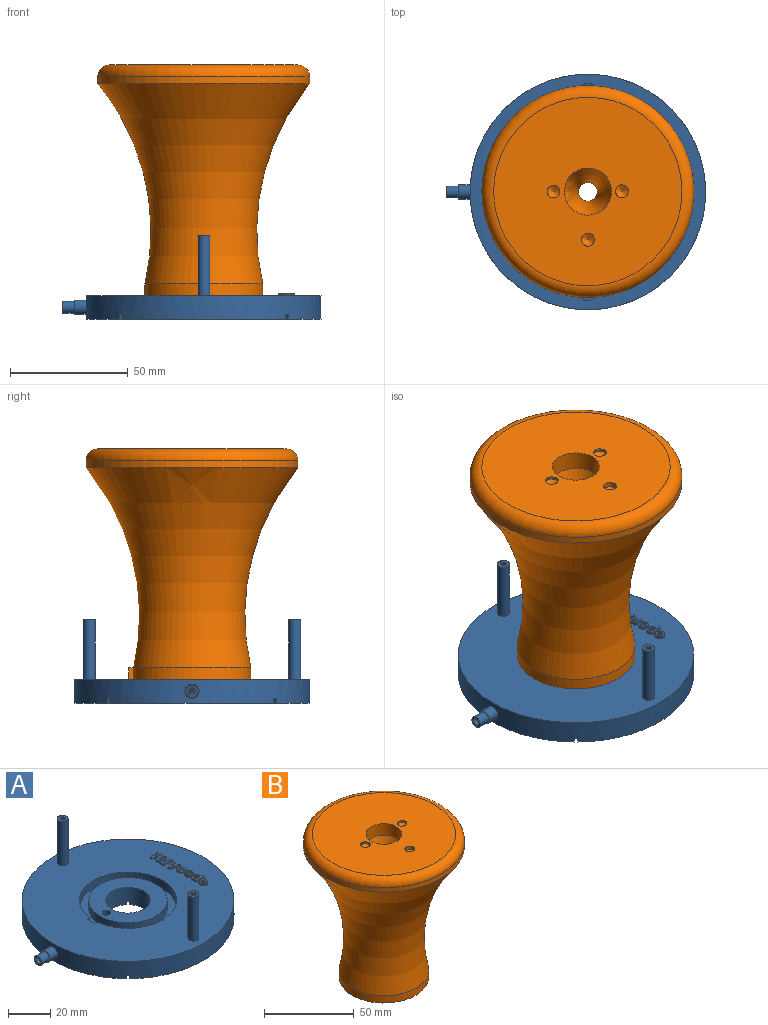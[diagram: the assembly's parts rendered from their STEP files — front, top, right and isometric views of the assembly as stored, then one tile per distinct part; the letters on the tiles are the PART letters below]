
ASSEMBLY  parts=2 mates=1
PART A: 135 faces, bbox 110x100x35.4 mm
  f0: plane 6.01x6.01mm, normal (-1,0,0), area 8.7mm2, adj f122,f123
  f1: cylinder r=50mm len=100mm, axis (0,0,-1), area 3101mm2, adj f3,f4,f5,f6,f7,f110,f111,f112
  f2: cylinder r=10.5mm len=21mm, axis (0,0,1), area 641.3mm2, adj f3,f4,f5,f6,f8,f110,f111,f112
  f3: plane 69.64x42.06mm, normal (0,0,-1), area 1817.6mm2, adj f1,f2,f117,f119
  f4: plane 69.64x42.06mm, normal (0,0,-1), area 1805.1mm2, adj f1,f2,f9,f113,f116
  f5: plane 69.64x42.06mm, normal (0,0,-1), area 1817.6mm2, adj f1,f2,f111,f120
  f6: plane 69.64x42.06mm, normal (0,0,-1), area 1817.6mm2, adj f1,f2,f110,f114
  f7: plane 100x100mm, normal (0,0,1), area 6049.5mm2, adj f1,f10,f11,f12,f13,f17,f18,f19
  f8: plane 37x37mm, normal (0,0,1), area 716.3mm2, adj f2,f9,f14
  f9: cylinder r=2mm len=10mm, axis (0,0,1), area 113.2mm2, adj f4,f8,f125,f126
  f10: cylinder r=23mm len=46mm, axis (0,0,1), area 697.5mm2, adj f7,f11,f13,f15
  f11: plane 5x1.64mm, normal (0,1,0), area 8.2mm2, adj f7,f10,f12,f15
  f12: plane 5x5mm, normal (1,0,0), area 25mm2, adj f7,f11,f13,f15
  f13: plane 5x1.64mm, normal (0,-1,0), area 8.2mm2, adj f7,f10,f12,f15
  f14: cylinder r=18.5mm len=37mm, axis (0,0,1), area 581.2mm2, adj f8,f15
  f15: plane 47.5x46mm, normal (0,0,1), area 594.4mm2, adj f10,f11,f12,f13,f14
  f16: plane 4.16x4.16mm, normal (0,0,1), area 9.6mm2, adj f17,f18,f19,f20,f21,f22,f23,f24
  f17: extruded ~1.37x1mm, area 1.5mm2, adj f7,f16,f18,f21
  f18: extruded ~1.54x1mm, area 1.7mm2, adj f7,f16,f17,f19
  f19: extruded ~2.08x2.06mm, area 3.3mm2, adj f7,f16,f18,f20
  f20: extruded ~2.1x2.08mm, area 3.3mm2, adj f7,f16,f19,f21
  f21: extruded ~2.1x2.08mm, area 3.3mm2, adj f7,f16,f17,f20
  f22: extruded ~1.16x1.1mm, area 1.8mm2, adj f16,f23,f25,f26
  f23: extruded ~1.16x1.09mm, area 1.8mm2, adj f16,f22,f24,f26
  f24: extruded ~1.17x1.09mm, area 1.8mm2, adj f16,f23,f25,f26
  f25: extruded ~1.17x1.1mm, area 1.8mm2, adj f16,f22,f24,f26
  f26: plane 2.33x2.19mm, normal (0,0,1), area 4.1mm2, adj f22,f23,f24,f25
  f27: plane 5.57x4.16mm, normal (0,0,1), area 12.4mm2, adj f28,f29,f30,f31,f32,f33,f34,f35
  f28: plane 1x0.99mm, normal (-1,0,0), area 1mm2, adj f7,f27,f29,f36
  f29: plane 5.5x1mm, normal (0,-1,0), area 5.5mm2, adj f7,f27,f28,f30
  f30: plane 1x0.99mm, normal (1,0,0), area 1mm2, adj f7,f27,f29,f31
  f31: plane 1.93x1mm, normal (0,1,0), area 1.9mm2, adj f7,f27,f30,f32
  f32: extruded ~1.25x1mm, area 1.4mm2, adj f7,f27,f31,f33
  f33: extruded ~2.07x1.93mm, area 3.1mm2, adj f7,f27,f32,f34
  f34: extruded ~2.09x1.9mm, area 3.2mm2, adj f7,f27,f33,f35
  f35: extruded ~1.28x1mm, area 1.4mm2, adj f7,f27,f34,f36
  f36: plane 1x0.45mm, normal (0,1,0), area 0.5mm2, adj f7,f27,f28,f35
  f37: extruded ~1.16x1.12mm, area 1.8mm2, adj f27,f38,f40,f41
  f38: extruded ~1.15x1.13mm, area 1.8mm2, adj f27,f37,f39,f41
  f39: extruded ~1.17x1.13mm, area 1.8mm2, adj f27,f38,f40,f41
  f40: extruded ~1.17x1.12mm, area 1.8mm2, adj f27,f37,f39,f41
  f41: plane 2.33x2.26mm, normal (0,0,1), area 4.2mm2, adj f37,f38,f39,f40
  f42: plane 4.16x4.16mm, normal (0,0,1), area 10.3mm2, adj f43,f44,f45,f46,f47,f48,f49,f50
  f43: plane 1x0.19mm, normal (0.02,1,0), area 0.2mm2, adj f7,f42,f44,f51
  f44: extruded ~2.14x2.11mm, area 3.4mm2, adj f7,f42,f43,f45
  f45: extruded ~2.1x2.05mm, area 3.3mm2, adj f7,f42,f44,f46
  f46: extruded ~2.1x2.06mm, area 3.3mm2, adj f7,f42,f45,f47
  f47: extruded ~1.78x1mm, area 2.1mm2, adj f7,f42,f46,f48
  f48: plane 1x0.83mm, normal (-0.9,0.43,0), area 0.9mm2, adj f7,f42,f47,f49
  f49: extruded ~1x0.94mm, area 1.1mm2, adj f7,f42,f48,f50
  f50: extruded ~1.12x1mm, area 1.6mm2, adj f7,f42,f49,f51
  f51: plane 3.17x1mm, normal (1,0,0), area 3.2mm2, adj f7,f42,f43,f50
  f52: plane 2.12x1mm, normal (-1,0,0), area 2.1mm2, adj f42,f53,f55,f56
  f53: extruded ~1.04x1mm, area 1.3mm2, adj f42,f52,f54,f56
  f54: extruded ~1x0.72mm, area 0.8mm2, adj f42,f53,f55,f56
  f55: extruded ~1x0.48mm, area 0.6mm2, adj f42,f52,f54,f56
  f56: plane 2.12x0.71mm, normal (0,0,1), area 1.1mm2, adj f52,f53,f54,f55
  f57: plane 4.02x1mm, normal (0,-1,0), area 4mm2, adj f7,f58,f70,f71
  f58: plane 1x0.99mm, normal (1,0,0), area 1mm2, adj f7,f57,f59,f71
  f59: plane 1.6x1mm, normal (0,1,0), area 1.6mm2, adj f7,f58,f60,f71
  f60: extruded ~1x0.81mm, area 0.8mm2, adj f7,f59,f61,f71
  f61: extruded ~1x0.86mm, area 1.3mm2, adj f7,f60,f62,f71
  f62: extruded ~1.43x1mm, area 1.8mm2, adj f7,f61,f63,f71
  f63: plane 1.75x1mm, normal (0,-1,0), area 1.7mm2, adj f7,f62,f64,f71
  f64: plane 1x0.99mm, normal (1,0,0), area 1mm2, adj f7,f63,f65,f71
  f65: plane 2.64x1mm, normal (0,1,0), area 2.6mm2, adj f7,f64,f66,f71
  f66: extruded ~1.04x1mm, area 1.1mm2, adj f7,f65,f67,f71
  f67: extruded ~1.03x1mm, area 1.1mm2, adj f7,f66,f68,f71
  f68: extruded ~1.22x1mm, area 1.3mm2, adj f7,f67,f69,f71
  f69: plane 1x0.43mm, normal (0,1,0), area 0.4mm2, adj f7,f68,f70,f71
  f70: plane 1x0.99mm, normal (-1,0,0), area 1mm2, adj f7,f57,f69,f71
  f71: plane 4.09x3.6mm, normal (0,0,1), area 9.2mm2, adj f57,f58,f59,f60,f61,f62,f63,f64
  f72: plane 5.5x5.36mm, normal (0,0,1), area 12.5mm2, adj f73,f74,f75,f76,f77,f78,f79,f80
  f73: plane 5.5x2.22mm, normal (-0.37,-0.93,0), area 5.9mm2, adj f7,f72,f74,f80
  f74: plane 1.05x1mm, normal (1,0,0), area 1.1mm2, adj f7,f72,f73,f75
  f75: plane 1.13x1mm, normal (0.35,0.94,0), area 1.2mm2, adj f7,f72,f74,f76
  f76: plane 2.4x1mm, normal (1,0,0), area 2.4mm2, adj f7,f72,f75,f77
  f77: plane 1.13x1mm, normal (0.35,-0.94,0), area 1.2mm2, adj f7,f72,f76,f78
  f78: plane 1.05x1mm, normal (1,0,0), area 1.1mm2, adj f7,f72,f77,f79
  f79: plane 5.5x2.22mm, normal (-0.37,0.93,0), area 5.9mm2, adj f7,f72,f78,f80
  f80: plane 1x0.92mm, normal (-1,0,0), area 0.9mm2, adj f7,f72,f73,f79
  f81: plane 1.91x1mm, normal (0.4,-0.92,0), area 2.1mm2, adj f72,f82,f83,f84
  f82: plane 1.91x1mm, normal (0.4,0.92,0), area 2.1mm2, adj f72,f81,f83,f84
  f83: plane 1.65x1mm, normal (-1,0,0), area 1.6mm2, adj f72,f81,f82,f84
  f84: plane 1.91x1.65mm, normal (0,0,1), area 1.6mm2, adj f81,f82,f83
  f85: plane 5.5x1mm, normal (0,-1,0), area 5.5mm2, adj f7,f86,f94,f95
  f86: plane 1x0.99mm, normal (1,0,0), area 1mm2, adj f7,f85,f87,f95
  f87: plane 2.47x1mm, normal (0,1,0), area 2.5mm2, adj f7,f86,f88,f95
  f88: plane 1.69x1mm, normal (1,0,0), area 1.7mm2, adj f7,f87,f89,f95
  f89: plane 1x0.99mm, normal (0,1,0), area 1mm2, adj f7,f88,f90,f95
  f90: plane 1.69x1mm, normal (-1,0,0), area 1.7mm2, adj f7,f89,f91,f95
  f91: plane 1.06x1mm, normal (0,1,0), area 1.1mm2, adj f7,f90,f92,f95
  f92: plane 1.69x1mm, normal (1,0,0), area 1.7mm2, adj f7,f91,f93,f95
  f93: plane 1x0.99mm, normal (0,1,0), area 1mm2, adj f7,f92,f94,f95
  f94: plane 2.68x1mm, normal (-1,0,0), area 2.7mm2, adj f7,f85,f93,f95
  f95: plane 5.5x2.68mm, normal (0,0,1), area 8.8mm2, adj f85,f86,f87,f88,f89,f90,f91,f92
  f96: plane 5.5x1mm, normal (-0.17,-0.99,0), area 5.6mm2, adj f7,f97,f108,f109
  f97: plane 1x1mm, normal (1,0,0), area 1mm2, adj f7,f96,f98,f109
  f98: plane 3.47x1mm, normal (0.17,0.99,0), area 3.5mm2, adj f7,f97,f99,f109
  f99: plane 3.47x1.14mm, normal (0.31,-0.95,0), area 3.7mm2, adj f7,f98,f100,f109
  f100: plane 1x0.96mm, normal (1,0,0), area 1mm2, adj f7,f99,f101,f109
  f101: plane 3.47x1.14mm, normal (0.31,0.95,0), area 3.7mm2, adj f7,f100,f102,f109
  f102: plane 3.47x1mm, normal (0.17,-0.99,0), area 3.5mm2, adj f7,f101,f103,f109
  f103: plane 1x1mm, normal (1,0,0), area 1mm2, adj f7,f102,f104,f109
  f104: plane 5.5x1mm, normal (-0.17,0.99,0), area 5.6mm2, adj f7,f103,f105,f109
  f105: plane 1.01x1mm, normal (-1,0,0), area 1mm2, adj f7,f104,f106,f109
  f106: plane 3.84x1.26mm, normal (-0.31,-0.95,0), area 4mm2, adj f7,f105,f107,f109
  f107: plane 3.84x1.26mm, normal (-0.31,0.95,0), area 4mm2, adj f7,f106,f108,f109
  f108: plane 1.02x1mm, normal (-1,0,0), area 1mm2, adj f7,f96,f107,f109
  f109: plane 6.42x5.5mm, normal (0,0,1), area 19.3mm2, adj f96,f97,f98,f99,f100,f101,f102,f103
  f110: plane 27.95x27.95mm, normal (0.71,0.71,0), area 79mm2, adj f1,f2,f6,f112
  f111: plane 27.95x27.95mm, normal (-0.71,-0.71,0), area 79mm2, adj f1,f2,f5,f112
  f112: plane 29.01x29.01mm, normal (0,0,-1), area 59.3mm2, adj f1,f2,f110,f111
  f113: plane 27.95x27.95mm, normal (0.71,-0.71,0), area 79mm2, adj f1,f2,f4,f115
  f114: plane 27.95x27.95mm, normal (-0.71,0.71,0), area 79mm2, adj f1,f2,f6,f115
  f115: plane 29.01x29.01mm, normal (0,0,-1), area 59.3mm2, adj f1,f2,f113,f114
  f116: plane 27.95x27.95mm, normal (0.71,0.71,0), area 79mm2, adj f1,f2,f4,f118
  f117: plane 27.95x27.95mm, normal (-0.71,-0.71,0), area 79mm2, adj f1,f2,f3,f118
  f118: plane 29.01x29.01mm, normal (0,0,-1), area 59.3mm2, adj f1,f2,f116,f117
  f119: plane 27.95x27.95mm, normal (0.71,-0.71,0), area 79mm2, adj f1,f2,f3,f121
  f120: plane 27.95x27.95mm, normal (-0.71,0.71,0), area 79mm2, adj f1,f2,f5,f121
  f121: plane 29.01x29.01mm, normal (0,0,-1), area 59.3mm2, adj f1,f2,f119,f120
  f122: cylinder r=3mm len=6.01mm, axis (1,0,0), area 96.1mm2, adj f0,f1
  f123: cylinder r=2.5mm len=5.01mm, axis (1,0,0), area 78.7mm2, adj f0,f124
  f124: plane 5.02x5.02mm, normal (-1,0,0), area 12.6mm2, adj f123,f125
  f125: bspline ~44.02x4.48mm, area 362.6mm2, adj f9,f124
  f126: bspline ~2.88x2.83mm, area 20.1mm2, adj f2,f9
  f127: cylinder r=1.27mm len=25.4mm, axis (0,0,-1), area 202.7mm2, adj f129,f130
  f128: cylinder r=2.58mm len=25.4mm, axis (0,0,-1), area 411.4mm2, adj f7,f129
  f129: plane 5.16x5.16mm, normal (0,0,1), area 15.8mm2, adj f127,f128
  f130: plane 2.54x2.54mm, normal (0,0,1), area 5.1mm2, adj f127
  f131: cylinder r=1.27mm len=25.4mm, axis (0,0,-1), area 202.7mm2, adj f133,f134
  f132: cylinder r=2.58mm len=25.4mm, axis (0,0,-1), area 411.4mm2, adj f7,f133
  f133: plane 5.16x5.16mm, normal (0,0,1), area 15.8mm2, adj f131,f132
  f134: plane 2.54x2.54mm, normal (0,0,1), area 5.1mm2, adj f131
PART B: 24 faces, bbox 110.4x110.4x146.7 mm
  f0: cylinder r=25mm len=50mm, axis (0,0,1), area 748.8mm2, adj f1,f4,f21,f22
  f1: plane 51.91x50mm, normal (0,0,-1), area 715.1mm2, adj f0,f5,f20,f21,f22
  f2: torus R=59.08mm, axis (0,0,-1), area 980.7mm2, adj f3,f8
  f3: cylinder r=4mm len=55mm, axis (0,0,-1), area 1382.3mm2, adj f2,f17
  f4: torus R=120.92mm, axis (0,0,-1), area 16143mm2, adj f0,f7,f19
  f5: cylinder r=20mm len=40mm, axis (0,0,-1), area 615.8mm2, adj f1,f6
  f6: plane 40x40mm, normal (0,0,-1), area 910.3mm2, adj f5,f18
  f7: cylinder r=45mm len=90mm, axis (0,0,-1), area 848.2mm2, adj f4,f10
  f8: cylinder r=10mm len=20mm, axis (0,0,-1), area 502.7mm2, adj f2,f9
  f9: plane 80x80mm, normal (0,0,1), area 4642.9mm2, adj f8,f10,f11,f13,f15
  f10: torus R=40mm, axis (0,0,-1), area 2131mm2, adj f7,f9
  f11: cylinder r=2.71mm len=5.43mm, axis (0,0,1), area 18.8mm2, adj f9,f12
  f12: cone r=0mm half-angle=59deg, axis (0,0,1), area 27mm2, adj f11
  f13: cylinder r=2.71mm len=5.43mm, axis (0,0,1), area 18.8mm2, adj f9,f14
  f14: cone r=0mm half-angle=59deg, axis (0,0,1), area 27mm2, adj f13
  f15: cylinder r=2.71mm len=5.43mm, axis (0,0,1), area 37.5mm2, adj f9,f16
  f16: cone r=0mm half-angle=59deg, axis (0,0,1), area 27mm2, adj f15
  f17: plane 21x21mm, normal (0,0,-1), area 296.1mm2, adj f3,f18
  f18: cylinder r=10.5mm len=21mm, axis (0,0,-1), area 329.9mm2, adj f6,f17
  f19: cylinder r=25mm len=4.25mm, axis (0,0,-1), area 0.4mm2, adj f4,f21,f22,f23
  f20: plane 5x4.25mm, normal (0,1,0), area 21.2mm2, adj f1,f21,f22,f23
  f21: plane 5x2mm, normal (1,0,0), area 10mm2, adj f0,f1,f19,f20,f23
  f22: plane 5x2mm, normal (-1,0,0), area 10mm2, adj f0,f1,f19,f20,f23
  f23: plane 4.25x2mm, normal (0,0,1), area 8.2mm2, adj f19,f20,f21,f22
PLACE A t=(39.35,107.76,6.2)mm
PLACE B t=(39.35,107.76,21.1)mm
MATE fastened B.f0 <-> A.f1  axis (0,0,-1) through (39.35,107.76,16.2)mm
